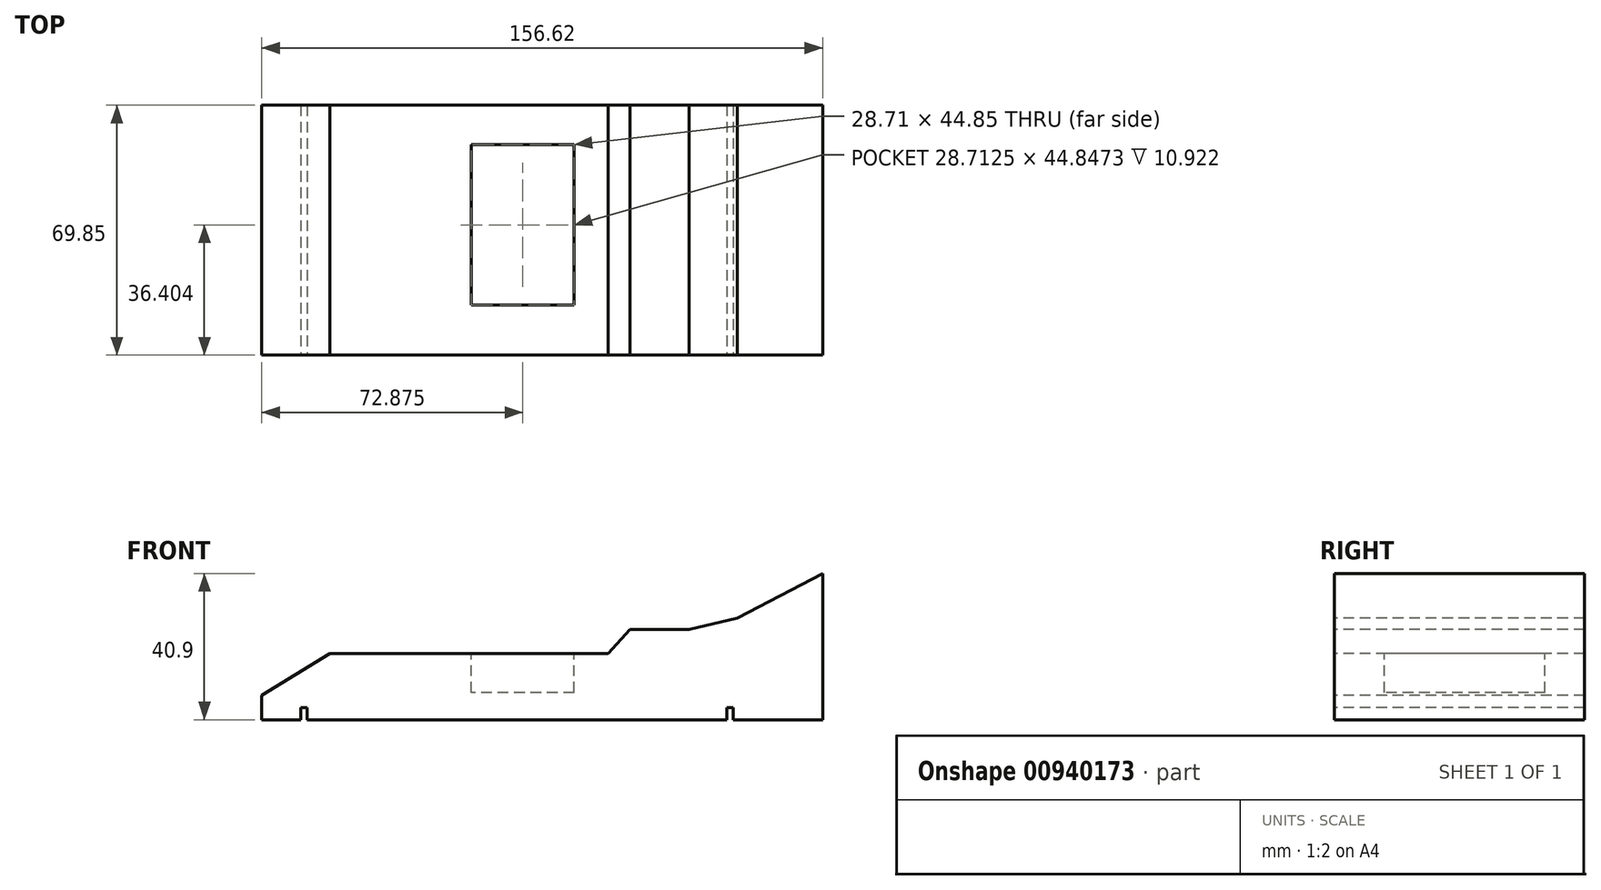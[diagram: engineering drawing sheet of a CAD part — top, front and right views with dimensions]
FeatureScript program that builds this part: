
annotation { "Feature Type Name" : "Feature", "Feature Type Description" : "" }
export const myFeature = defineFeature(function(context is Context, id is Id, definition is map)
    precondition{}
    {
        {
            var Q0;
            Q0=qCreatedBy(makeId("Top.planeOp"),FACE);
            var sketch = newSketch(context, id + "F0", { "sketchPlane" : qUnion([Q0])});
            skLineSegment(sketch, "E0.bottom", {"start": v(78.3, -34.93) * mm, "end": v(-78.3, -34.93) * mm});
            skLineSegment(sketch, "E0.top", {"start": v(78.3, 34.93) * mm, "end": v(-78.3, 34.93) * mm});
            skLineSegment(sketch, "E0.left", {"start": v(78.3, -34.93) * mm, "end": v(78.3, 34.92) * mm});
            skLineSegment(sketch, "E0.right", {"start": v(-78.3, -34.93) * mm, "end": v(-78.3, 34.92) * mm});
            skPoint(sketch, "E0.middle", {"position": v(0, 0) * mm});
            skSolve(sketch);
        }
        {
            var Q0;
            Q0 = qSketchRegion(id + "F0", true);
            extrude(context, id + "F1", {"entities" : qUnion([Q0]), "depth" : 50.8 * mm, "offsetDistance" : 25.4 * mm});
        }
        {
            var Q0;
            Q0=makeQuery(id+"F1.opExtrude","SWEPT_FACE",FACE,{"disambiguationData":[OSD([sQuery(id+"F0.wireOp",EDGE,"E0.bottom")])]});
            var sketch = newSketch(context, id + "F2", { "sketchPlane" : qUnion([Q0])});
            skLineSegment(sketch, "E1", {"start": v(-80.43, 5.48) * mm, "end": v(-59.35, 18.55) * mm});
            skLineSegment(sketch, "E2", {"start": v(-59.35, 18.55) * mm, "end": v(-30.25, 18.55) * mm});
            skLineSegment(sketch, "E3", {"start": v(-30.25, 18.55) * mm, "end": v(18.45, 18.55) * mm});
            skLineSegment(sketch, "E4", {"start": v(18.45, 18.55) * mm, "end": v(24.56, 25.3) * mm});
            skLineSegment(sketch, "E5", {"start": v(24.56, 25.3) * mm, "end": v(41, 25.3) * mm});
            skLineSegment(sketch, "E6", {"start": v(41, 25.3) * mm, "end": v(54.5, 28.46) * mm});
            skLineSegment(sketch, "E7", {"start": v(54.5, 28.46) * mm, "end": v(78.3, 40.9) * mm});
            skLineSegment(sketch, "E8", {"start": v(78.3, 40.9) * mm, "end": v(84.02, 52.7) * mm});
            skLineSegment(sketch, "E9", {"start": v(84.02, 52.7) * mm, "end": v(-62.09, 67.68) * mm});
            skLineSegment(sketch, "E10", {"start": v(-62.09, 67.68) * mm, "end": v(-96.24, 45.54) * mm});
            skLineSegment(sketch, "E11", {"start": v(-96.24, 45.54) * mm, "end": v(-80.43, 5.48) * mm});
            skSolve(sketch);
        }
        {
            var Q0;
            Q0 = qSketchRegion(id + "F2", true);
            extrude(context, id + "F3", {"entities" : qUnion([Q0]), "operationType" : NewBodyOperationType.REMOVE, "oppositeDirection" : true, "depth" : 90.42 * mm, "offsetDistance" : 25.4 * mm});
        }
        {
            var Q0;
            Q0=makeQuery(id+"F3.boolean.opBoolean","COPY",FACE,{"derivedFrom":makeQuery(id+"F3.opExtrude","SWEPT_FACE",FACE,{"disambiguationData":[OSD([sQuery(id+"F2.wireOp",EDGE,"E2"),sQuery(id+"F2.wireOp",EDGE,"E3")])]})});
            var sketch = newSketch(context, id + "F4", { "sketchPlane" : qUnion([Q0])});
            skLineSegment(sketch, "E12", {"start": v(-19.8, 23.9) * mm, "end": v(-19.8, -20.95) * mm});
            skLineSegment(sketch, "E13", {"start": v(-19.8, -20.95) * mm, "end": v(8.92, -20.95) * mm});
            skLineSegment(sketch, "E14", {"start": v(8.92, -20.95) * mm, "end": v(8.92, 23.9) * mm});
            skLineSegment(sketch, "E15", {"start": v(8.92, 23.9) * mm, "end": v(-19.8, 23.9) * mm});
            skSolve(sketch);
        }
        {
            var Q0;
            Q0 = qSketchRegion(id + "F4", true);
            extrude(context, id + "F5", {"entities" : qUnion([Q0]), "operationType" : NewBodyOperationType.REMOVE, "oppositeDirection" : true, "depth" : 10.92 * mm, "offsetDistance" : 25.4 * mm});
        }
        {
            var Q0;
            Q0=makeQuery(id+"F1.opExtrude","SWEPT_FACE",FACE,{"disambiguationData":[OSD([sQuery(id+"F0.wireOp",EDGE,"E0.bottom")])]});
            var sketch = newSketch(context, id + "F6", { "sketchPlane" : qUnion([Q0])});
            skLineSegment(sketch, "E16.bottom", {"start": v(-67.4, 3.35) * mm, "end": v(-65.64, 3.35) * mm});
            skLineSegment(sketch, "E16.top", {"start": v(-67.4, -3.28) * mm, "end": v(-65.64, -3.28) * mm});
            skLineSegment(sketch, "E16.left", {"start": v(-67.4, 3.35) * mm, "end": v(-67.4, -3.28) * mm});
            skLineSegment(sketch, "E16.right", {"start": v(-65.64, 3.35) * mm, "end": v(-65.64, -3.28) * mm});
            skSolve(sketch);
        }
        {
            var Q0;
            Q0 = qSketchRegion(id + "F6", true);
            extrude(context, id + "F7", {"entities" : qUnion([Q0]), "operationType" : NewBodyOperationType.REMOVE, "oppositeDirection" : true, "depth" : 123.16 * mm, "offsetDistance" : 25.4 * mm});
        }
        {
            var Q0;
            Q0=makeQuery(id+"F1.opExtrude","SWEPT_FACE",FACE,{"disambiguationData":[OSD([sQuery(id+"F0.wireOp",EDGE,"E0.bottom")])]});
            var sketch = newSketch(context, id + "F8", { "sketchPlane" : qUnion([Q0])});
            skLineSegment(sketch, "E17.bottom", {"start": v(51.53, 3.35) * mm, "end": v(53.28, 3.35) * mm});
            skLineSegment(sketch, "E17.top", {"start": v(51.53, -5.15) * mm, "end": v(53.28, -5.15) * mm});
            skLineSegment(sketch, "E17.left", {"start": v(51.53, 3.35) * mm, "end": v(51.53, -5.15) * mm});
            skLineSegment(sketch, "E17.right", {"start": v(53.28, 3.35) * mm, "end": v(53.28, -5.15) * mm});
            skSolve(sketch);
        }
        {
            var Q0;
            Q0 = qSketchRegion(id + "F8", true);
            extrude(context, id + "F9", {"entities" : qUnion([Q0]), "operationType" : NewBodyOperationType.REMOVE, "oppositeDirection" : true, "depth" : 74.78 * mm, "offsetDistance" : 25.4 * mm});
        }
    });
